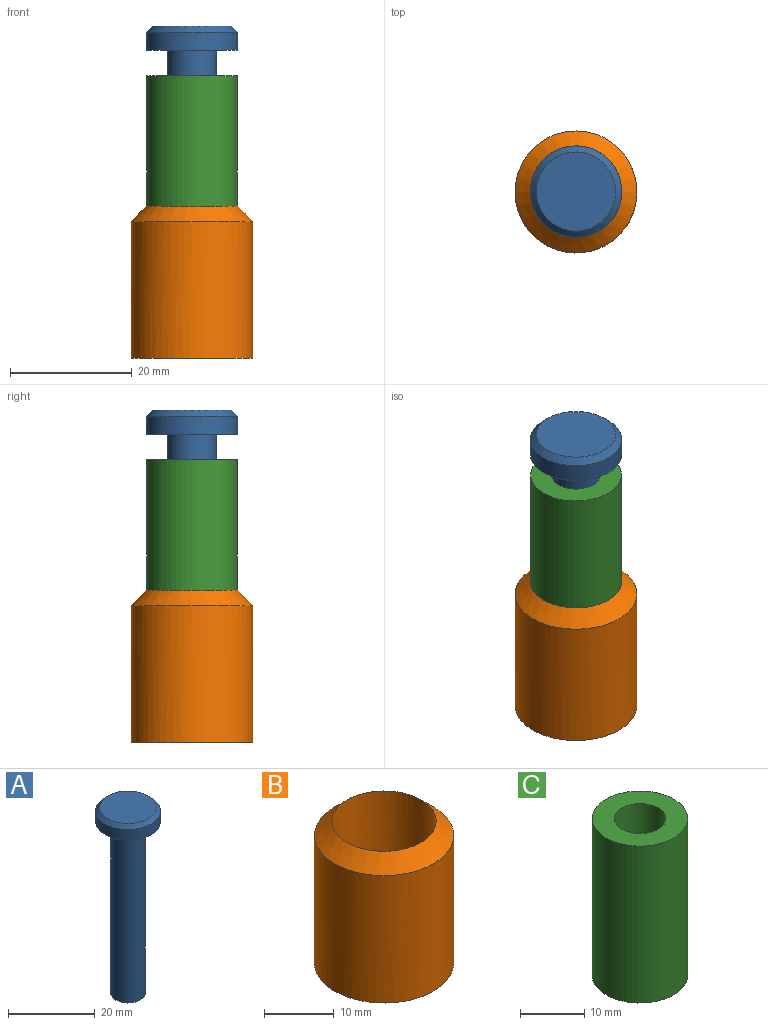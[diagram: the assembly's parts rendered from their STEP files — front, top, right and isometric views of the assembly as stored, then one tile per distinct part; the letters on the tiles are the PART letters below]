
ASSEMBLY  parts=3 mates=2
PART A: 6 faces, bbox 15x15x52.5 mm
  f0: cylinder r=4mm len=48.5mm, axis (0,0,-1), area 1218.9mm2, adj f1,f3
  f1: plane 8x8mm, normal (0,0,-1), area 50.3mm2, adj f0
  f2: cylinder r=7.5mm len=15mm, axis (0,0,1), area 141.4mm2, adj f3,f5
  f3: plane 15x15mm, normal (0,0,-1), area 126.4mm2, adj f0,f2
  f4: plane 13x13mm, normal (0,0,1), area 132.7mm2, adj f5
  f5: cone r=6.5mm half-angle=45deg, axis (0,0,-1), area 62.2mm2, adj f2,f4
PART B: 9 faces, bbox 20x20x24.9 mm
  f0: cylinder r=7.5mm len=15.9mm, axis (0,0,-1), area 749.3mm2, adj f3,f4
  f1: cylinder r=10mm len=22.4mm, axis (0,0,-1), area 1407.4mm2, adj f2,f4
  f2: plane 20x20mm, normal (0,0,-1), area 201.1mm2, adj f1,f5
  f3: plane 15x15mm, normal (0,0,1), area 138.4mm2, adj f0,f8
  f4: cone r=7.4mm half-angle=45deg, axis (0,0,-1), area 194.4mm2, adj f0,f1
  f5: cylinder r=6mm len=12mm, axis (0,0,-1), area 75.4mm2, adj f2,f6
  f6: plane 12x12mm, normal (0,0,-1), area 84.8mm2, adj f5,f7
  f7: cylinder r=3mm len=6.51mm, axis (0,0,-1), area 122.7mm2, adj f6,f8
  f8: cone r=3mm half-angle=45deg, axis (0,0,1), area 14.2mm2, adj f3,f7
PART C: 4 faces, bbox 14.9x14.9x30 mm
  f0: cylinder r=4.05mm len=30mm, axis (0,0,1), area 763.4mm2, adj f2,f3
  f1: cylinder r=7.45mm len=30mm, axis (0,0,1), area 1404.3mm2, adj f2,f3
  f2: plane 14.9x14.9mm, normal (0,0,-1), area 122.8mm2, adj f0,f1
  f3: plane 14.9x14.9mm, normal (0,0,1), area 122.8mm2, adj f0,f1
PLACE A t=(0,0,-0.5)mm
PLACE B at identity
PLACE C t=(0,0,-4.64)mm
MATE slider C.f0 <-> A.f2  axis (0,0,1) through (0,0,46.36)mm
MATE fastened A.f0 <-> B.f7  axis (0,0,-1) through (0,0,2)mm
